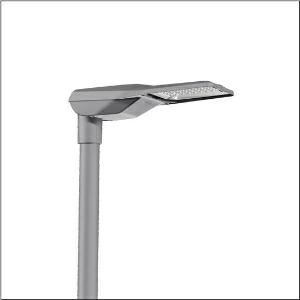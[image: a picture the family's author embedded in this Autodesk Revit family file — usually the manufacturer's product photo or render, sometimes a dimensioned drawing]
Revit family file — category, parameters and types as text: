
# Revit family: streetlight_sl_21_iq_mini___st1_5a_5xe2p41d08gb_b9bd
name_source: partatom
category: Lighting Fixtures
units: mm (PartAtom-declared; Revit-internal decimal feet)

## family parameters
Cut with Voids When Loaded = No
Host = Face
Light Source = No
Part Type = Normal
Room Calculation Point = No
Round Connector Dimension = Use Diameter
Shared = No

## types (1)
- --- (1 x LED, 5810 lm, 37.1 W, 4000K)
    Apparent Load = 37 VA
    CIE Flux Codes = 22 53 95 100 100
    Color Rendering = 70
    Color Temperature = 4000K
    Default Elevation = 1800 mm
    Description = Streetlight SL 21 iQ mini, mast luminaire, primary light control with lens, of PMMA, primary optical cover: cover, of toughened safety glass, transparent, light distribution: ST1.5a, light emission: direct distribution, primary light characteristic: asymmetric, installation type: post-top, side-entry, LED, High Power LED, rated luminous flux: 5.810lm, luminous efficacy: 157lm/W, light colour: 740, colour temperature: 4000K, control: Auto-Match, Temp-Guard, Lumen-Switch, Night-Set, Smart-Wire, Light-Fading, Desk-Remote (wireless, voltage-free reading and setting of iQ features in the workshop via application-optimized NFC function/RFID function), optimised constant luminous flux control (CLO 2.0), presetting dimming linear, mains connection: 220..240V, AC, 50/60Hz, start of lifetime: 37W, end of service life: 39W, reduction: 18W, luminaire housing, of diecast aluminium, powder-coated, Siteco® metallic grey (DB 702S), corrosivity category C5 mid according to DIN EN ISO 12944, please order mast flange separately, inclination adjustable: 0°, 5°, 10°, 15°, sealing non-destructively replaceable, multi-level sealing system, length: 628mm, width: 235mm, height: 110mm, mast flange for spigot size: 42mm (side-entry): 5XC10008XM4, 60/48mm (side-entry/post-top): 5XC10108XM2, 76/60mm (side-entry/post-top): 5XC10108XM1, protection rating (complete): IP66, insulation class (complete): insulation class II (safety insulation), certification: CE, ENEC, ENEC+, VDE, impact resistance: IK09, permissible operating ambient temperature for outdoor applications: -40..+50°C, standard-compliant lighting for roads and squares, packaging unit: 1 piece

Light Distribution: ST1.5a
    Height = 110 mm
    Lamp = 1 x LED
    Lamp Light Flux = 5810 lm
    Lamp Power = 37.1 W
    Lamp count = 1
    Length = 625 mm
    Luminous efficacy = 157 lm/W
    Manufacturer = Siteco
    ModVariant = No
    Model = 5XE2P41D08GB
    Number of Poles = 1
    OnlyDefault = Yes
    Power Factor = 1
    Product Name = Streetlight SL 21 iQ mini | ST1.5a
    Product group = mast luminaire | pylon top
    ProductGroupID = 6100
    Protection Class = Protection class II
    Protection Degree = IP 66
    RLX_Detail_Level = 1
    RLX_Emergency_Light_Flux = 0 lm
    RLX_Emergency_Type = 0
    RLX_Emergency_Type_DB = No
    RlxData = <blob elided: 96397 chars, md5=54e7e2a7>
    Socket = socket
    Standby Power = 0 W
    System Light Flux = 5810 lm
    System Power = 37 W
    Type Comments = factory setting: luminous flux: 100 % | dim-lin: 254 | 385 mA
    Type Image = l_1003519.jpg
    URL = http://relux.com
    VarID = @adj_109011
    Voltage = 0 V
    Weight = 0.00 kg
    Width = 234 mm

## geometry (parser evidence)
native form markers: Blend x4, Sweep x9
no freeform markers — native parametric forms only
